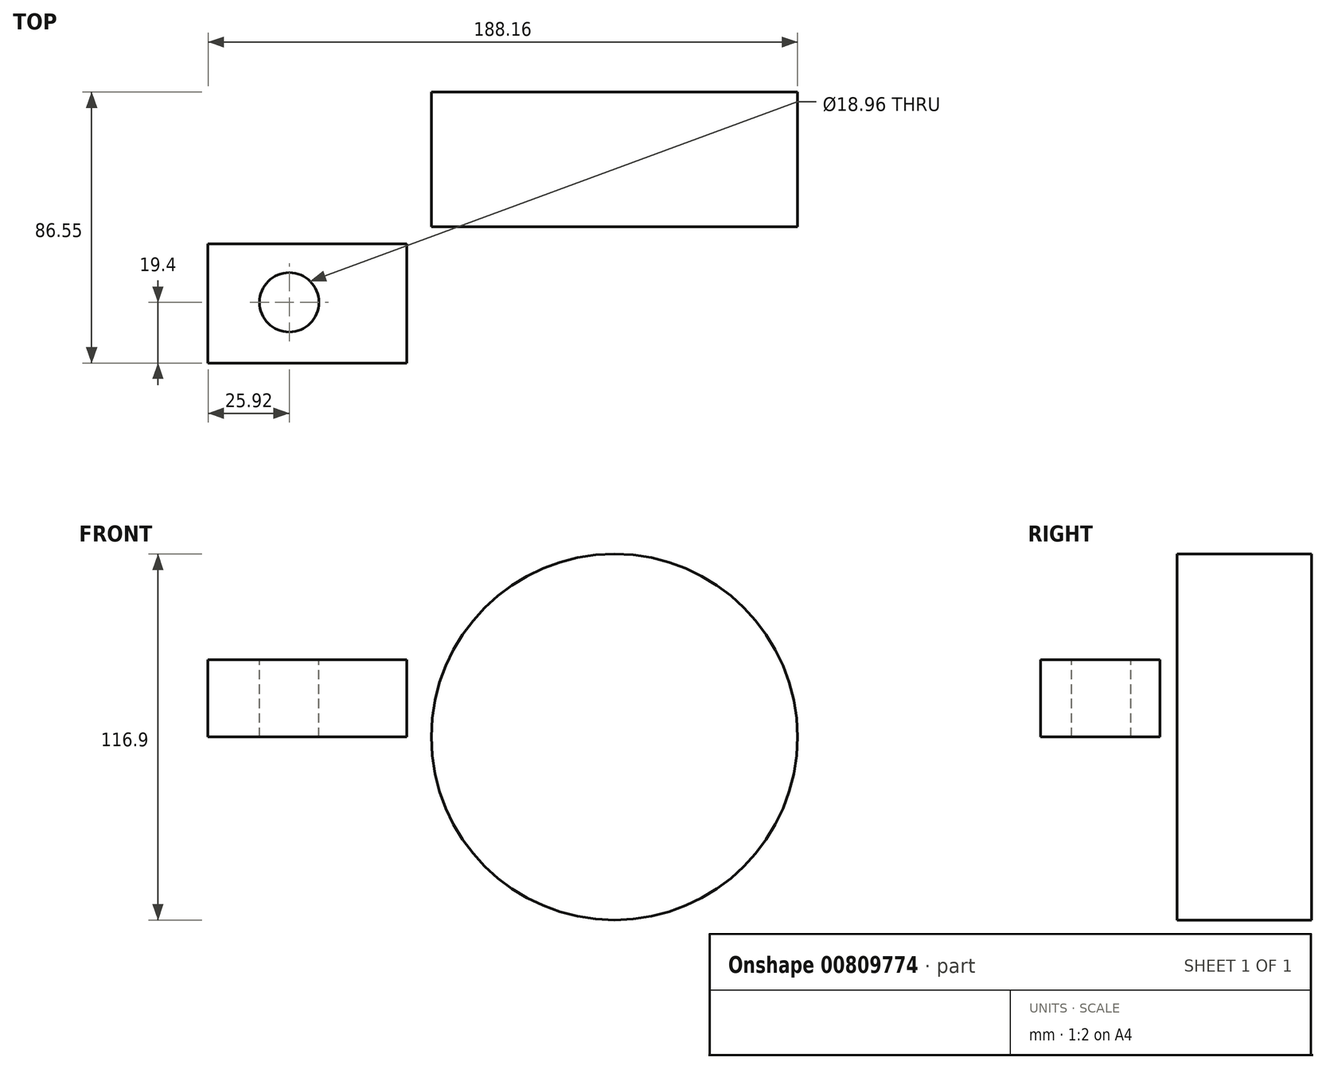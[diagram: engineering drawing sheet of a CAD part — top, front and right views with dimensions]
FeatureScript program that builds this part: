
annotation { "Feature Type Name" : "Feature", "Feature Type Description" : "" }
export const myFeature = defineFeature(function(context is Context, id is Id, definition is map)
    precondition{}
    {
        {
            var Q0;
            Q0=qCreatedBy(makeId("Top.planeOp"),FACE);
            var sketch = newSketch(context, id + "F0", { "sketchPlane" : qUnion([Q0])});
            skLineSegment(sketch, "E0.bottom", {"start": v(15.1, -24.97) * mm, "end": v(73.56, -24.97) * mm});
            skLineSegment(sketch, "E0.top", {"start": v(15.1, 17.99) * mm, "end": v(73.56, 17.99) * mm});
            skLineSegment(sketch, "E0.left", {"start": v(15.1, -24.97) * mm, "end": v(15.1, 17.99) * mm});
            skLineSegment(sketch, "E0.right", {"start": v(73.56, -24.97) * mm, "end": v(73.56, 17.99) * mm});
            skSolve(sketch);
        }
        {
            var Q0;
            Q0 = qSketchRegion(id + "F0", true);
            var Q1;
            Q1=sQuery(id+"F0.wireOp",EDGE,"E0.left");
            revolve(context, id + "F1", {"surfaceOperationType" : NewSurfaceOperationType.NEW, "entities" : qUnion([Q0]), "axis" : qUnion([Q1]), "revolveType" : RevolveType.FULL});
        }
        {
            var Q0;
            Q0=qCreatedBy(makeId("Top.planeOp"),FACE);
            var sketch = newSketch(context, id + "F2", { "sketchPlane" : qUnion([Q0])});
            skLineSegment(sketch, "E1.bottom", {"start": v(-114.6, -30.46) * mm, "end": v(-51.1, -30.46) * mm});
            skLineSegment(sketch, "E1.top", {"start": v(-114.6, -68.56) * mm, "end": v(-51.1, -68.56) * mm});
            skLineSegment(sketch, "E1.left", {"start": v(-114.6, -30.46) * mm, "end": v(-114.6, -68.56) * mm});
            skLineSegment(sketch, "E1.right", {"start": v(-51.1, -30.46) * mm, "end": v(-51.1, -68.56) * mm});
            skSolve(sketch);
        }
        {
            var Q0;
            Q0=makeQuery(id+"F2.imprint","IMPRINT",FACE,{"disambiguationData":[TD([[makeQuery(id+"F2.imprint","IMPRINT",EDGE,{"derivedFrom":sQuery(id+"F2.wireOp",EDGE,"E1.bottom")}),-1.0]])]});
            extrude(context, id + "F3", {"entities" : qUnion([Q0]), "depth" : 24.64 * mm, "offsetDistance" : 25.4 * mm});
        }
        {
            var Q0;
            Q0=makeQuery(id+"F3.opExtrude","CAP_FACE",FACE,{"disambiguationData":[OSD([sQuery(id+"F2.wireOp",EDGE,"E1.bottom"),sQuery(id+"F2.wireOp",EDGE,"E1.top"),sQuery(id+"F2.wireOp",EDGE,"E1.left"),sQuery(id+"F2.wireOp",EDGE,"E1.right")])],"isStart":false});
            var sketch = newSketch(context, id + "F4", { "sketchPlane" : qUnion([Q0])});
            skCircle(sketch, "E2", {"center": v(-88.68, -49.16) * mm, "radius": 9.48 * mm});
            skSolve(sketch);
        }
        {
            var Q0;
            Q0=makeQuery(id+"F4.imprint","IMPRINT",FACE,{"disambiguationData":[TD([[makeQuery(id+"F4.imprint","IMPRINT",EDGE,{"derivedFrom":sQuery(id+"F4.wireOp",EDGE,"E2")}),1.0]])]});
            extrude(context, id + "F5", {"entities" : qUnion([Q0]), "operationType" : NewBodyOperationType.REMOVE, "oppositeDirection" : true, "depth" : 72.14 * mm, "offsetDistance" : 25.4 * mm});
        }
    });
